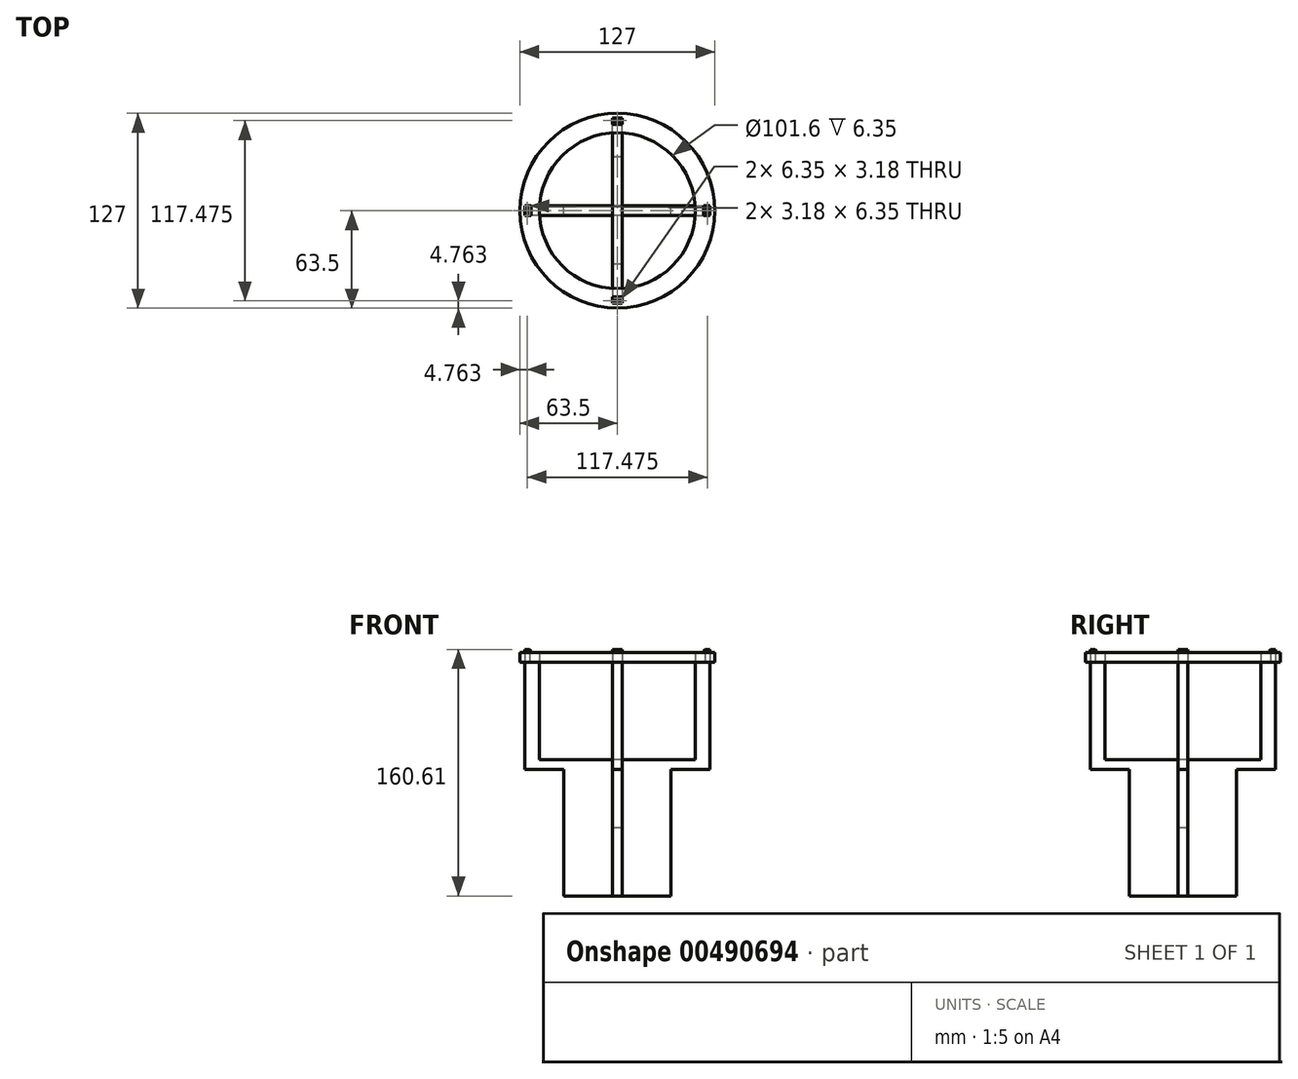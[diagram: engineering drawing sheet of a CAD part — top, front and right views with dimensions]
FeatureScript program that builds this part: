
annotation { "Feature Type Name" : "Feature", "Feature Type Description" : "" }
export const myFeature = defineFeature(function(context is Context, id is Id, definition is map)
    precondition{}
    {
        {
            var Q0;
            Q0=qCreatedBy(makeId("Front.planeOp"),FACE);
            var sketch = newSketch(context, id + "F0", { "sketchPlane" : qUnion([Q0])});
            skLineSegment(sketch, "E0", {"start": v(0, -82.55) * mm, "end": v(34.93, -82.55) * mm});
            skLineSegment(sketch, "E1", {"start": v(34.92, -82.55) * mm, "end": v(34.92, 0) * mm});
            skLineSegment(sketch, "E2", {"start": v(50.8, 6.35) * mm, "end": v(3.18, 6.35) * mm});
            skLineSegment(sketch, "E3", {"start": v(0, 6.35) * mm, "end": v(0, -82.55) * mm, "construction": true});
            skLineSegment(sketch, "E4", {"start": v(3.18, -38.1) * mm, "end": v(3.18, 6.35) * mm});
            skPoint(sketch, "E5.orphan", {"position": v(0, 6.35) * mm});
            skLineSegment(sketch, "E6", {"start": v(50.8, 6.35) * mm, "end": v(50.8, 69.85) * mm});
            skLineSegment(sketch, "E7", {"start": v(50.8, 69.85) * mm, "end": v(60.32, 69.85) * mm});
            skLineSegment(sketch, "E8", {"start": v(60.32, 69.85) * mm, "end": v(60.32, 0) * mm});
            skLineSegment(sketch, "E9", {"start": v(34.92, 0) * mm, "end": v(60.33, 0) * mm});
            skLineSegment(sketch, "E10", {"start": v(60.32, 69.85) * mm, "end": v(60.32, 78.06) * mm});
            skLineSegment(sketch, "E11", {"start": v(60.32, 78.06) * mm, "end": v(57.15, 78.06) * mm});
            skLineSegment(sketch, "E12", {"start": v(57.15, 78.06) * mm, "end": v(56.22, 77.19) * mm});
            skLineSegment(sketch, "E13", {"start": v(56.22, 77.19) * mm, "end": v(57.15, 76.2) * mm});
            skLineSegment(sketch, "E14", {"start": v(57.15, 76.2) * mm, "end": v(57.15, 69.85) * mm});
            skLineSegment(sketch, "E15.MirrorCS", {"start": v(-60.33, 78.06) * mm, "end": v(-57.15, 78.06) * mm});
            skLineSegment(sketch, "E16.MirrorCS", {"start": v(-57.15, 78.06) * mm, "end": v(-56.22, 77.19) * mm});
            skLineSegment(sketch, "E17.MirrorCS", {"start": v(-60.33, 69.85) * mm, "end": v(-60.33, 78.06) * mm});
            skLineSegment(sketch, "E18.MirrorCS", {"start": v(-57.15, 76.2) * mm, "end": v(-57.15, 69.85) * mm});
            skLineSegment(sketch, "E19.MirrorCS", {"start": v(-56.22, 77.19) * mm, "end": v(-57.15, 76.2) * mm});
            skLineSegment(sketch, "E20.MirrorCS", {"start": v(-50.8, 69.85) * mm, "end": v(-60.33, 69.85) * mm});
            skLineSegment(sketch, "E21.MirrorCS", {"start": v(-60.33, 69.85) * mm, "end": v(-60.33, 0) * mm});
            skLineSegment(sketch, "E22.MirrorCS", {"start": v(-34.92, -82.55) * mm, "end": v(-34.92, 0) * mm});
            skLineSegment(sketch, "E23.MirrorCS", {"start": v(0, -82.55) * mm, "end": v(-34.92, -82.55) * mm});
            skLineSegment(sketch, "E24.MirrorCS", {"start": v(-50.8, 6.35) * mm, "end": v(-50.8, 69.85) * mm});
            skLineSegment(sketch, "E25.MirrorCS", {"start": v(-3.18, -38.1) * mm, "end": v(-3.18, 6.35) * mm});
            skLineSegment(sketch, "E26.MirrorCS", {"start": v(-34.92, 0) * mm, "end": v(-60.33, 0) * mm});
            skLineSegment(sketch, "E27.MirrorCS", {"start": v(-50.8, 6.35) * mm, "end": v(-3.18, 6.35) * mm});
            skLineSegment(sketch, "E28", {"start": v(-3.18, -38.1) * mm, "end": v(3.18, -38.1) * mm});
            skSolve(sketch);
        }
        {
            var Q0;
            Q0=makeQuery(id+"F0.imprint","IMPRINT",FACE,{"disambiguationData":[TD([[makeQuery(id+"F0.imprint","IMPRINT",EDGE,{"derivedFrom":sQuery(id+"F0.wireOp",EDGE,"E0")}),1.0]])]});
            var Q1;
            Q1=makeQuery(id+"F0.imprint","IMPRINT",FACE,{"disambiguationData":[TD([[makeQuery(id+"F0.imprint","IMPRINT",EDGE,{"derivedFrom":sQuery(id+"F0.wireOp",EDGE,"4bfa33b7-be46-4f8e-9b05-16dc533d22064.MirrorCS")}),1.0]])]});
            var Q2;
            Q2=makeQuery(id+"F0.imprint","IMPRINT",FACE,{"disambiguationData":[TD([[makeQuery(id+"F0.imprint","IMPRINT",EDGE,{"derivedFrom":sQuery(id+"F0.wireOp",EDGE,"16HsfyeY-BBUm-mBOU-ZyVs-EQiSUkY2iwHP")}),-1.0]])]});
            var Q3;
            Q3=makeQuery(id+"F0.imprint","IMPRINT",FACE,{"disambiguationData":[TD([[makeQuery(id+"F0.imprint","IMPRINT",EDGE,{"derivedFrom":sQuery(id+"F0.wireOp",EDGE,"E15.MirrorCS")}),-1.0]])]});
            var Q4;
            {var subQ0=sQuery(id+"F0.wireOp",EDGE,"E10");Q4=makeQuery(id+"F0.imprint","IMPRINT",FACE,{"disambiguationData":[TD([[makeQuery(id+"F0.imprint","IMPRINT",EDGE,{"derivedFrom":subQ0}),1.0]])]});}
            extrude(context, id + "F1", {"entities" : qUnion([Q0, Q1, Q2, Q3, Q4]), "endBound" : BoundingType.SYMMETRIC, "depth" : 6.35 * mm});
        }
        {
            var Q0;
            Q0=qCreatedBy(makeId("Right.planeOp"),FACE);
            var sketch = newSketch(context, id + "F2", { "sketchPlane" : qUnion([Q0])});
            skLineSegment(sketch, "E29", {"start": v(0, -82.55) * mm, "end": v(34.93, -82.55) * mm});
            skLineSegment(sketch, "E30", {"start": v(34.93, -82.55) * mm, "end": v(34.93, 0) * mm});
            skLineSegment(sketch, "E31", {"start": v(50.8, 6.35) * mm, "end": v(3.18, 6.35) * mm});
            skLineSegment(sketch, "E32", {"start": v(0, 6.35) * mm, "end": v(0, -82.55) * mm, "construction": true});
            skPoint(sketch, "E33.orphan", {"position": v(0, 6.35) * mm});
            skLineSegment(sketch, "E34", {"start": v(0, -38.1) * mm, "end": v(0, -38.1) * mm});
            skLineSegment(sketch, "E35", {"start": v(50.8, 6.35) * mm, "end": v(50.8, 69.85) * mm});
            skLineSegment(sketch, "E36", {"start": v(50.8, 69.85) * mm, "end": v(60.33, 69.85) * mm});
            skLineSegment(sketch, "E37", {"start": v(60.33, 69.85) * mm, "end": v(60.33, 0) * mm});
            skLineSegment(sketch, "E38", {"start": v(34.93, 0) * mm, "end": v(60.33, 0) * mm});
            skLineSegment(sketch, "E39", {"start": v(60.33, 69.85) * mm, "end": v(60.33, 78.06) * mm});
            skLineSegment(sketch, "E40", {"start": v(60.33, 78.06) * mm, "end": v(57.15, 78.06) * mm});
            skLineSegment(sketch, "E41", {"start": v(57.15, 78.06) * mm, "end": v(56.22, 77.19) * mm});
            skLineSegment(sketch, "E42", {"start": v(56.22, 77.19) * mm, "end": v(57.15, 76.2) * mm});
            skLineSegment(sketch, "E43", {"start": v(57.15, 76.2) * mm, "end": v(57.15, 69.85) * mm});
            skLineSegment(sketch, "E44.MirrorCS", {"start": v(-60.33, 78.06) * mm, "end": v(-57.15, 78.06) * mm});
            skLineSegment(sketch, "E45.MirrorCS", {"start": v(-57.15, 78.06) * mm, "end": v(-56.22, 77.19) * mm});
            skLineSegment(sketch, "E46.MirrorCS", {"start": v(-60.33, 69.85) * mm, "end": v(-60.33, 78.06) * mm});
            skLineSegment(sketch, "E47.MirrorCS", {"start": v(-57.15, 76.2) * mm, "end": v(-57.15, 69.85) * mm});
            skLineSegment(sketch, "E48.MirrorCS", {"start": v(-56.22, 77.19) * mm, "end": v(-57.15, 76.2) * mm});
            skLineSegment(sketch, "E49.MirrorCS", {"start": v(-50.8, 69.85) * mm, "end": v(-60.33, 69.85) * mm});
            skLineSegment(sketch, "E50.MirrorCS", {"start": v(-60.33, 69.85) * mm, "end": v(-60.33, 0) * mm});
            skLineSegment(sketch, "E51.MirrorCS", {"start": v(-34.92, -82.55) * mm, "end": v(-34.93, 0) * mm});
            skLineSegment(sketch, "E52.MirrorCS", {"start": v(0, -82.55) * mm, "end": v(-34.92, -82.55) * mm});
            skLineSegment(sketch, "E53.MirrorCS", {"start": v(-50.8, 6.35) * mm, "end": v(-50.8, 69.85) * mm});
            skLineSegment(sketch, "E54.MirrorCS", {"start": v(-34.93, 0) * mm, "end": v(-60.33, 0) * mm});
            skLineSegment(sketch, "E55.MirrorCS", {"start": v(-50.8, 6.35) * mm, "end": v(-3.18, 6.35) * mm});
            skLineSegment(sketch, "E56", {"start": v(0, -38.1) * mm, "end": v(0, -82.55) * mm});
            skLineSegment(sketch, "E57", {"start": v(3.18, 6.35) * mm, "end": v(-3.18, 6.35) * mm});
            skPoint(sketch, "E58.orphan", {"position": v(0, -82.55) * mm});
            skLineSegment(sketch, "E59", {"start": v(0, -38.1) * mm, "end": v(-3.17, -38.1) * mm});
            skLineSegment(sketch, "E60", {"start": v(-3.17, -38.1) * mm, "end": v(-3.17, -82.55) * mm});
            skLineSegment(sketch, "E61", {"start": v(0, -38.1) * mm, "end": v(3.18, -38.1) * mm});
            skLineSegment(sketch, "E62", {"start": v(3.18, -38.1) * mm, "end": v(3.18, -82.55) * mm});
            skSolve(sketch);
        }
        {
            var Q0;
            {var subQ9=sQuery(id+"F2.wireOp",EDGE,"E30");Q0=makeQuery(id+"F2.imprint","IMPRINT",FACE,{"disambiguationData":[TD([[makeQuery(id+"F2.imprint","IMPRINT",EDGE,{"derivedFrom":subQ9}),1.0]])]});}
            var Q1;
            {var subQ0=sQuery(id+"F2.wireOp",EDGE,"E39");Q1=makeQuery(id+"F2.imprint","IMPRINT",FACE,{"disambiguationData":[TD([[makeQuery(id+"F2.imprint","IMPRINT",EDGE,{"derivedFrom":subQ0}),1.0]])]});}
            var Q2;
            Q2=makeQuery(id+"F2.imprint","IMPRINT",FACE,{"disambiguationData":[TD([[makeQuery(id+"F2.imprint","IMPRINT",EDGE,{"derivedFrom":sQuery(id+"F2.wireOp",EDGE,"E44.MirrorCS")}),-1.0]])]});
            extrude(context, id + "F3", {"entities" : qUnion([Q0, Q1, Q2]), "endBound" : BoundingType.SYMMETRIC, "depth" : 6.35 * mm});
        }
        {
            var Q0;
            Q0=makeQuery(id+"F3.opExtrude","SWEPT_FACE",FACE,{"disambiguationData":[OSD([sQuery(id+"F2.wireOp",EDGE,"E36")])]});
            var sketch = newSketch(context, id + "F4", { "sketchPlane" : qUnion([Q0])});
            skCircle(sketch, "E63", {"center": v(0, 0) * mm, "radius": 63.5 * mm});
            skCircle(sketch, "E64", {"center": v(0, 0) * mm, "radius": 50.8 * mm});
            skLineSegment(sketch, "E65.bottom", {"start": v(3.17, 60.33) * mm, "end": v(-3.18, 60.33) * mm});
            skLineSegment(sketch, "E65.top", {"start": v(3.17, 57.15) * mm, "end": v(-3.18, 57.15) * mm});
            skLineSegment(sketch, "E65.left", {"start": v(3.17, 60.33) * mm, "end": v(3.17, 57.15) * mm});
            skLineSegment(sketch, "E65.right", {"start": v(-3.18, 60.33) * mm, "end": v(-3.18, 57.15) * mm});
            skPoint(sketch, "E65.middle", {"position": v(0, 58.74) * mm});
            skLineSegment(sketch, "E66.1.0", {"start": v(-60.33, -3.18) * mm, "end": v(-57.15, -3.18) * mm});
            skPoint(sketch, "E66.1.1", {"position": v(-58.74, 0) * mm});
            skLineSegment(sketch, "E66.1.2", {"start": v(-57.15, 3.17) * mm, "end": v(-57.15, -3.18) * mm});
            skLineSegment(sketch, "E66.1.3", {"start": v(-60.33, 3.17) * mm, "end": v(-60.33, -3.18) * mm});
            skLineSegment(sketch, "E66.1.4", {"start": v(-60.33, 3.17) * mm, "end": v(-57.15, 3.17) * mm});
            skLineSegment(sketch, "E66.2.0", {"start": v(3.17, -60.33) * mm, "end": v(3.17, -57.15) * mm});
            skPoint(sketch, "E66.2.1", {"position": v(0, -58.74) * mm});
            skLineSegment(sketch, "E66.2.2", {"start": v(-3.18, -57.15) * mm, "end": v(3.17, -57.15) * mm});
            skLineSegment(sketch, "E66.2.3", {"start": v(-3.18, -60.33) * mm, "end": v(3.17, -60.33) * mm});
            skLineSegment(sketch, "E66.2.4", {"start": v(-3.18, -60.33) * mm, "end": v(-3.18, -57.15) * mm});
            skLineSegment(sketch, "E66.3.0", {"start": v(60.33, 3.17) * mm, "end": v(57.15, 3.17) * mm});
            skPoint(sketch, "E66.3.1", {"position": v(58.74, 0) * mm});
            skLineSegment(sketch, "E66.3.2", {"start": v(57.15, -3.18) * mm, "end": v(57.15, 3.17) * mm});
            skLineSegment(sketch, "E66.3.3", {"start": v(60.33, -3.18) * mm, "end": v(60.33, 3.17) * mm});
            skLineSegment(sketch, "E66.3.4", {"start": v(60.33, -3.18) * mm, "end": v(57.15, -3.18) * mm});
            skSolve(sketch);
        }
        {
            var Q0;
            Q0=makeQuery(id+"F4.imprint","IMPRINT",FACE,{"disambiguationData":[TD([[makeQuery(id+"F4.imprint","IMPRINT",EDGE,{"derivedFrom":sQuery(id+"F4.wireOp",EDGE,"E63")}),1.0]])]});
            var Q1;
            Q1=makeQuery(id+"F4.imprint","IMPRINT",FACE,{"disambiguationData":[TD([[makeQuery(id+"F4.imprint","IMPRINT",EDGE,{"derivedFrom":sQuery(id+"F4.wireOp",EDGE,"E65.top")}),1.0]])]});
            extrude(context, id + "F5", {"entities" : qUnion([Q0, Q1]), "depth" : 6.35 * mm});
        }
    });
